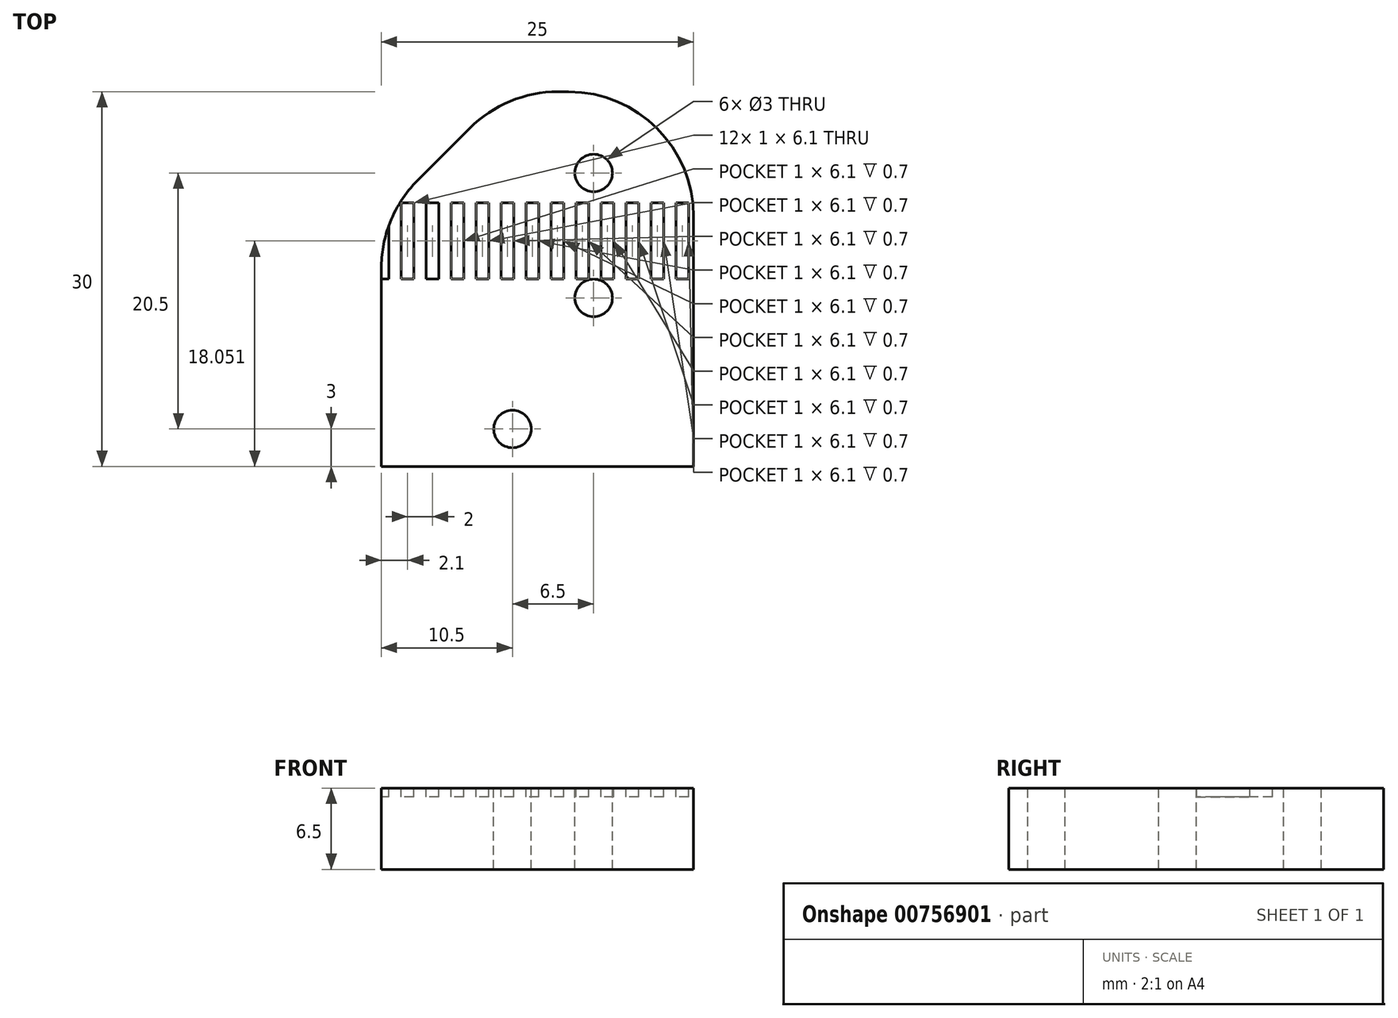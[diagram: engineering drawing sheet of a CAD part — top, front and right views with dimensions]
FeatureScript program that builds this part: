
annotation { "Feature Type Name" : "Feature", "Feature Type Description" : "" }
export const myFeature = defineFeature(function(context is Context, id is Id, definition is map)
    precondition{}
    {
        {
            var Q0;
            Q0=qCreatedBy(makeId("Top.planeOp"),FACE);
            var sketch = newSketch(context, id + "F0", { "sketchPlane" : qUnion([Q0])});
            skLineSegment(sketch, "E0.bottom", {"start": v(12.5, -15) * mm, "end": v(-12.5, -15) * mm});
            skLineSegment(sketch, "E0.top", {"start": v(12.5, 15) * mm, "end": v(-12.5, 15) * mm});
            skLineSegment(sketch, "E0.left", {"start": v(12.5, -15) * mm, "end": v(12.5, 15) * mm});
            skLineSegment(sketch, "E0.right", {"start": v(-12.5, -15) * mm, "end": v(-12.5, 15) * mm});
            skPoint(sketch, "E0.middle", {"position": v(0, 0) * mm});
            skSolve(sketch);
        }
        {
            var Q0;
            Q0=makeQuery(id+"F0.imprint","IMPRINT",FACE,{"disambiguationData":[TD([[makeQuery(id+"F0.imprint","IMPRINT",EDGE,{"derivedFrom":sQuery(id+"F0.wireOp",EDGE,"E0.bottom")}),-1.0]])]});
            extrude(context, id + "F1", {"entities" : qUnion([Q0]), "depth" : 6.5 * mm, "offsetDistance" : 25 * mm});
        }
        {
            var Q0;
            Q0=makeQuery(id+"F1.opExtrude","CAP_FACE",FACE,{"disambiguationData":[OSD([sQuery(id+"F0.wireOp",EDGE,"E0.bottom"),sQuery(id+"F0.wireOp",EDGE,"E0.top"),sQuery(id+"F0.wireOp",EDGE,"E0.left"),sQuery(id+"F0.wireOp",EDGE,"E0.right")])],"isStart":false});
            var sketch = newSketch(context, id + "F2", { "sketchPlane" : qUnion([Q0])});
            skCircle(sketch, "E1", {"center": v(-2, -12) * mm, "radius": 1.5 * mm});
            skPoint(sketch, "E1.centerSnap0", {"position": v(0, -15) * mm});
            skCircle(sketch, "E2", {"center": v(4.5, -1.5) * mm, "radius": 1.5 * mm});
            skCircle(sketch, "E3", {"center": v(4.5, 8.5) * mm, "radius": 1.5 * mm});
            skSolve(sketch);
        }
        {
            var Q0;
            Q0=qSketchRegion(id+"F2",true);
            extrude(context, id + "F3", {"entities" : qUnion([Q0]), "operationType" : NewBodyOperationType.REMOVE, "endBound" : BoundingType.THROUGH_ALL, "oppositeDirection" : true, "depth" : 25 * mm, "offsetDistance" : 25 * mm});
        }
        {
            var Q0;
            Q0=makeQuery(id+"F1.opExtrude","CAP_FACE",FACE,{"disambiguationData":[OSD([sQuery(id+"F0.wireOp",EDGE,"E0.bottom"),sQuery(id+"F0.wireOp",EDGE,"E0.top"),sQuery(id+"F0.wireOp",EDGE,"E0.left"),sQuery(id+"F0.wireOp",EDGE,"E0.right")])],"isStart":false});
            var sketch = newSketch(context, id + "F4", { "sketchPlane" : qUnion([Q0])});
            skLineSegment(sketch, "E4.bottom", {"start": v(12.1, 0) * mm, "end": v(11.1, 0) * mm});
            skLineSegment(sketch, "E4.top", {"start": v(12.1, 6.1) * mm, "end": v(11.1, 6.1) * mm});
            skLineSegment(sketch, "E4.left", {"start": v(12.1, 0) * mm, "end": v(12.1, 6.1) * mm});
            skLineSegment(sketch, "E4.right", {"start": v(11.1, 0) * mm, "end": v(11.1, 6.1) * mm});
            skPoint(sketch, "E4.middle", {"position": v(11.6, 3.05) * mm});
            skLineSegment(sketch, "E5.bottom", {"start": v(10.1, 0) * mm, "end": v(9.1, 0) * mm});
            skLineSegment(sketch, "E5.top", {"start": v(10.1, 6.1) * mm, "end": v(9.1, 6.1) * mm});
            skLineSegment(sketch, "E5.left", {"start": v(10.1, 0) * mm, "end": v(10.1, 6.1) * mm});
            skLineSegment(sketch, "E5.right", {"start": v(9.1, 0) * mm, "end": v(9.1, 6.1) * mm});
            skPoint(sketch, "E5.middle", {"position": v(9.6, 3.05) * mm});
            skLineSegment(sketch, "E6.bottom", {"start": v(8.1, 0) * mm, "end": v(7.1, 0) * mm});
            skLineSegment(sketch, "E6.top", {"start": v(8.1, 6.1) * mm, "end": v(7.1, 6.1) * mm});
            skLineSegment(sketch, "E6.left", {"start": v(8.1, 0) * mm, "end": v(8.1, 6.1) * mm});
            skLineSegment(sketch, "E6.right", {"start": v(7.1, 0) * mm, "end": v(7.1, 6.1) * mm});
            skPoint(sketch, "E6.middle", {"position": v(7.6, 3.05) * mm});
            skLineSegment(sketch, "E7.bottom", {"start": v(6.1, 0) * mm, "end": v(5.1, 0) * mm});
            skLineSegment(sketch, "E7.top", {"start": v(6.1, 6.1) * mm, "end": v(5.1, 6.1) * mm});
            skLineSegment(sketch, "E7.left", {"start": v(6.1, 0) * mm, "end": v(6.1, 6.1) * mm});
            skLineSegment(sketch, "E7.right", {"start": v(5.1, 0) * mm, "end": v(5.1, 6.1) * mm});
            skPoint(sketch, "E7.middle", {"position": v(5.6, 3.05) * mm});
            skLineSegment(sketch, "E8.bottom", {"start": v(4.1, 0) * mm, "end": v(3.1, 0) * mm});
            skLineSegment(sketch, "E8.top", {"start": v(4.1, 6.1) * mm, "end": v(3.1, 6.1) * mm});
            skLineSegment(sketch, "E8.left", {"start": v(4.1, 0) * mm, "end": v(4.1, 6.1) * mm});
            skLineSegment(sketch, "E8.right", {"start": v(3.1, 0) * mm, "end": v(3.1, 6.1) * mm});
            skPoint(sketch, "E8.middle", {"position": v(3.6, 3.05) * mm});
            skLineSegment(sketch, "E9.bottom", {"start": v(2.1, 0) * mm, "end": v(1.1, 0) * mm});
            skLineSegment(sketch, "E9.top", {"start": v(2.1, 6.1) * mm, "end": v(1.1, 6.1) * mm});
            skLineSegment(sketch, "E9.left", {"start": v(2.1, 0) * mm, "end": v(2.1, 6.1) * mm});
            skLineSegment(sketch, "E9.right", {"start": v(1.1, 0) * mm, "end": v(1.1, 6.1) * mm});
            skPoint(sketch, "E9.middle", {"position": v(1.6, 3.05) * mm});
            skLineSegment(sketch, "E10.bottom", {"start": v(0.1, 0) * mm, "end": v(-0.9, 0) * mm});
            skLineSegment(sketch, "E10.top", {"start": v(0.1, 6.1) * mm, "end": v(-0.9, 6.1) * mm});
            skLineSegment(sketch, "E10.left", {"start": v(0.1, 0) * mm, "end": v(0.1, 6.1) * mm});
            skLineSegment(sketch, "E10.right", {"start": v(-0.9, 0) * mm, "end": v(-0.9, 6.1) * mm});
            skPoint(sketch, "E10.middle", {"position": v(-0.4, 3.05) * mm});
            skLineSegment(sketch, "E11", {"start": v(-12.5, 0) * mm, "end": v(12.5, 0) * mm, "construction": true});
            skLineSegment(sketch, "E12", {"start": v(12.5, 6.1) * mm, "end": v(-12.5, 6.1) * mm, "construction": true});
            skLineSegment(sketch, "E13.bottom", {"start": v(-1.9, 0) * mm, "end": v(-2.9, 0) * mm});
            skLineSegment(sketch, "E13.top", {"start": v(-1.9, 6.1) * mm, "end": v(-2.9, 6.1) * mm});
            skLineSegment(sketch, "E13.left", {"start": v(-1.9, 0) * mm, "end": v(-1.9, 6.1) * mm});
            skLineSegment(sketch, "E13.right", {"start": v(-2.9, 0) * mm, "end": v(-2.9, 6.1) * mm});
            skLineSegment(sketch, "E14.bottom", {"start": v(-3.9, 0) * mm, "end": v(-4.9, 0) * mm});
            skLineSegment(sketch, "E14.top", {"start": v(-3.9, 6.1) * mm, "end": v(-4.9, 6.1) * mm});
            skLineSegment(sketch, "E14.left", {"start": v(-3.9, 0) * mm, "end": v(-3.9, 6.1) * mm});
            skLineSegment(sketch, "E14.right", {"start": v(-4.9, 0) * mm, "end": v(-4.9, 6.1) * mm});
            skLineSegment(sketch, "E15.bottom", {"start": v(-5.9, 6.1) * mm, "end": v(-6.9, 6.1) * mm});
            skLineSegment(sketch, "E15.top", {"start": v(-5.9, 0) * mm, "end": v(-6.9, 0) * mm});
            skLineSegment(sketch, "E15.left", {"start": v(-5.9, 6.1) * mm, "end": v(-5.9, 0) * mm});
            skLineSegment(sketch, "E15.right", {"start": v(-6.9, 6.1) * mm, "end": v(-6.9, 0) * mm});
            skLineSegment(sketch, "E16.bottom", {"start": v(-7.9, 0) * mm, "end": v(-8.9, 0) * mm});
            skLineSegment(sketch, "E16.top", {"start": v(-7.9, 6.1) * mm, "end": v(-8.9, 6.1) * mm});
            skLineSegment(sketch, "E16.left", {"start": v(-7.9, 0) * mm, "end": v(-7.9, 6.1) * mm});
            skLineSegment(sketch, "E16.right", {"start": v(-8.9, 0) * mm, "end": v(-8.9, 6.1) * mm});
            skLineSegment(sketch, "E17.bottom", {"start": v(-9.9, 6.1) * mm, "end": v(-10.9, 6.1) * mm});
            skLineSegment(sketch, "E17.top", {"start": v(-9.9, 0) * mm, "end": v(-10.9, 0) * mm});
            skLineSegment(sketch, "E17.left", {"start": v(-9.9, 6.1) * mm, "end": v(-9.9, 0) * mm});
            skLineSegment(sketch, "E17.right", {"start": v(-10.9, 6.1) * mm, "end": v(-10.9, 0) * mm});
            skLineSegment(sketch, "E18.bottom", {"start": v(-11.9, 0) * mm, "end": v(-12.9, 0) * mm});
            skLineSegment(sketch, "E18.top", {"start": v(-11.9, 6.1) * mm, "end": v(-12.9, 6.1) * mm});
            skLineSegment(sketch, "E18.left", {"start": v(-11.9, 0) * mm, "end": v(-11.9, 6.1) * mm});
            skLineSegment(sketch, "E18.right", {"start": v(-12.9, 0) * mm, "end": v(-12.9, 6.1) * mm});
            skSolve(sketch);
        }
        {
            var Q0;
            Q0=makeQuery(id+"F4.imprint","IMPRINT",FACE,{"disambiguationData":[TD([[makeQuery(id+"F4.imprint","IMPRINT",EDGE,{"derivedFrom":sQuery(id+"F4.wireOp",EDGE,"E4.bottom")}),-1.0]])]});
            var Q1;
            Q1=makeQuery(id+"F4.imprint","IMPRINT",FACE,{"disambiguationData":[TD([[makeQuery(id+"F4.imprint","IMPRINT",EDGE,{"derivedFrom":sQuery(id+"F4.wireOp",EDGE,"E5.bottom")}),-1.0]])]});
            var Q2;
            Q2=makeQuery(id+"F4.imprint","IMPRINT",FACE,{"disambiguationData":[TD([[makeQuery(id+"F4.imprint","IMPRINT",EDGE,{"derivedFrom":sQuery(id+"F4.wireOp",EDGE,"E6.bottom")}),-1.0]])]});
            var Q3;
            Q3=makeQuery(id+"F4.imprint","IMPRINT",FACE,{"disambiguationData":[TD([[makeQuery(id+"F4.imprint","IMPRINT",EDGE,{"derivedFrom":sQuery(id+"F4.wireOp",EDGE,"E7.bottom")}),-1.0]])]});
            var Q4;
            Q4=makeQuery(id+"F4.imprint","IMPRINT",FACE,{"disambiguationData":[TD([[makeQuery(id+"F4.imprint","IMPRINT",EDGE,{"derivedFrom":sQuery(id+"F4.wireOp",EDGE,"E8.bottom")}),-1.0]])]});
            var Q5;
            Q5=makeQuery(id+"F4.imprint","IMPRINT",FACE,{"disambiguationData":[TD([[makeQuery(id+"F4.imprint","IMPRINT",EDGE,{"derivedFrom":sQuery(id+"F4.wireOp",EDGE,"E9.bottom")}),-1.0]])]});
            var Q6;
            Q6=makeQuery(id+"F4.imprint","IMPRINT",FACE,{"disambiguationData":[TD([[makeQuery(id+"F4.imprint","IMPRINT",EDGE,{"derivedFrom":sQuery(id+"F4.wireOp",EDGE,"E10.bottom")}),-1.0]])]});
            var Q7;
            Q7=makeQuery(id+"F4.imprint","IMPRINT",FACE,{"disambiguationData":[TD([[makeQuery(id+"F4.imprint","IMPRINT",EDGE,{"derivedFrom":sQuery(id+"F4.wireOp",EDGE,"E13.bottom")}),-1.0]])]});
            var Q8;
            Q8=makeQuery(id+"F4.imprint","IMPRINT",FACE,{"disambiguationData":[TD([[makeQuery(id+"F4.imprint","IMPRINT",EDGE,{"derivedFrom":sQuery(id+"F4.wireOp",EDGE,"E14.bottom")}),-1.0]])]});
            var Q9;
            Q9=makeQuery(id+"F4.imprint","IMPRINT",FACE,{"disambiguationData":[TD([[makeQuery(id+"F4.imprint","IMPRINT",EDGE,{"derivedFrom":sQuery(id+"F4.wireOp",EDGE,"E15.bottom")}),1.0]])]});
            var Q10;
            Q10=makeQuery(id+"F4.imprint","IMPRINT",FACE,{"disambiguationData":[TD([[makeQuery(id+"F4.imprint","IMPRINT",EDGE,{"derivedFrom":sQuery(id+"F4.wireOp",EDGE,"E16.bottom")}),-1.0]])]});
            var Q11;
            Q11=makeQuery(id+"F4.imprint","IMPRINT",FACE,{"disambiguationData":[TD([[makeQuery(id+"F4.imprint","IMPRINT",EDGE,{"derivedFrom":sQuery(id+"F4.wireOp",EDGE,"E17.bottom")}),1.0]])]});
            var Q12;
            {var subQ0=sQuery(id+"F4.wireOp",EDGE,"E18.right");Q12=makeQuery(id+"F4.imprint","IMPRINT",FACE,{"disambiguationData":[TD([[makeQuery(id+"F4.imprint","IMPRINT",EDGE,{"derivedFrom":subQ0}),-1.0]])]});}
            var Q13;
            {var subQ0=sQuery(id+"F4.wireOp",EDGE,"E18.left");Q13=makeQuery(id+"F4.imprint","IMPRINT",FACE,{"disambiguationData":[TD([[makeQuery(id+"F4.imprint","IMPRINT",EDGE,{"derivedFrom":subQ0}),1.0]])]});}
            extrude(context, id + "F5", {"entities" : qUnion([Q0, Q1, Q2, Q3, Q4, Q5, Q6, Q7, Q8, Q9, Q10, Q11, Q12, Q13]), "operationType" : NewBodyOperationType.REMOVE, "oppositeDirection" : true, "depth" : 0.7 * mm, "offsetDistance" : 25 * mm});
        }
        {
            var Q0;
            Q0=makeQuery(id+"F1.opExtrude","SWEPT_EDGE",EDGE,{"disambiguationData":[OSD([sQuery(id+"F0.wireOp",EDGE,"E0.top"),sQuery(id+"F0.wireOp",EDGE,"E0.right")])]});
            chamfer(context, id + "F6", {"entities" : qUnion([Q0]), "width" : 10 * mm, "tangentPropagation" : true});
        }
        {
            var Q0;
            {var subQ0=sQuery(id+"F0.wireOp",EDGE,"E0.top");Q0=makeQuery(id+"F6.opChamfer","BLEND_EDGE",EDGE,{"blendedFrom":[makeQuery(id+"F1.opExtrude","SWEPT_EDGE",EDGE,{"disambiguationData":[OSD([subQ0,sQuery(id+"F0.wireOp",EDGE,"E0.right")])]}),makeQuery(id+"F1.opExtrude","SWEPT_FACE",FACE,{"disambiguationData":[OSD([subQ0])]})],"blendedInto":[makeQuery(id+"F1.opExtrude","SWEPT_FACE",FACE,{"disambiguationData":[OSD([subQ0])]})]});}
            var Q1;
            {var subQ0=sQuery(id+"F0.wireOp",EDGE,"E0.right");Q1=makeQuery(id+"F6.opChamfer","BLEND_EDGE",EDGE,{"blendedFrom":[makeQuery(id+"F1.opExtrude","SWEPT_EDGE",EDGE,{"disambiguationData":[OSD([sQuery(id+"F0.wireOp",EDGE,"E0.top"),subQ0])]}),makeQuery(id+"F1.opExtrude","SWEPT_FACE",FACE,{"disambiguationData":[OSD([subQ0])]})],"blendedInto":[makeQuery(id+"F1.opExtrude","SWEPT_FACE",FACE,{"disambiguationData":[OSD([subQ0])]})]});}
            var Q2;
            Q2=makeQuery(id+"F1.opExtrude","SWEPT_EDGE",EDGE,{"disambiguationData":[OSD([sQuery(id+"F0.wireOp",EDGE,"E0.top"),sQuery(id+"F0.wireOp",EDGE,"E0.left")])]});
            fillet(context, id + "F7", {"entities" : qUnion([Q0, Q1, Q2]), "radius" : 10 * mm, "tangentPropagation" : true, "allowEdgeOverflow" : false});
        }
    });
